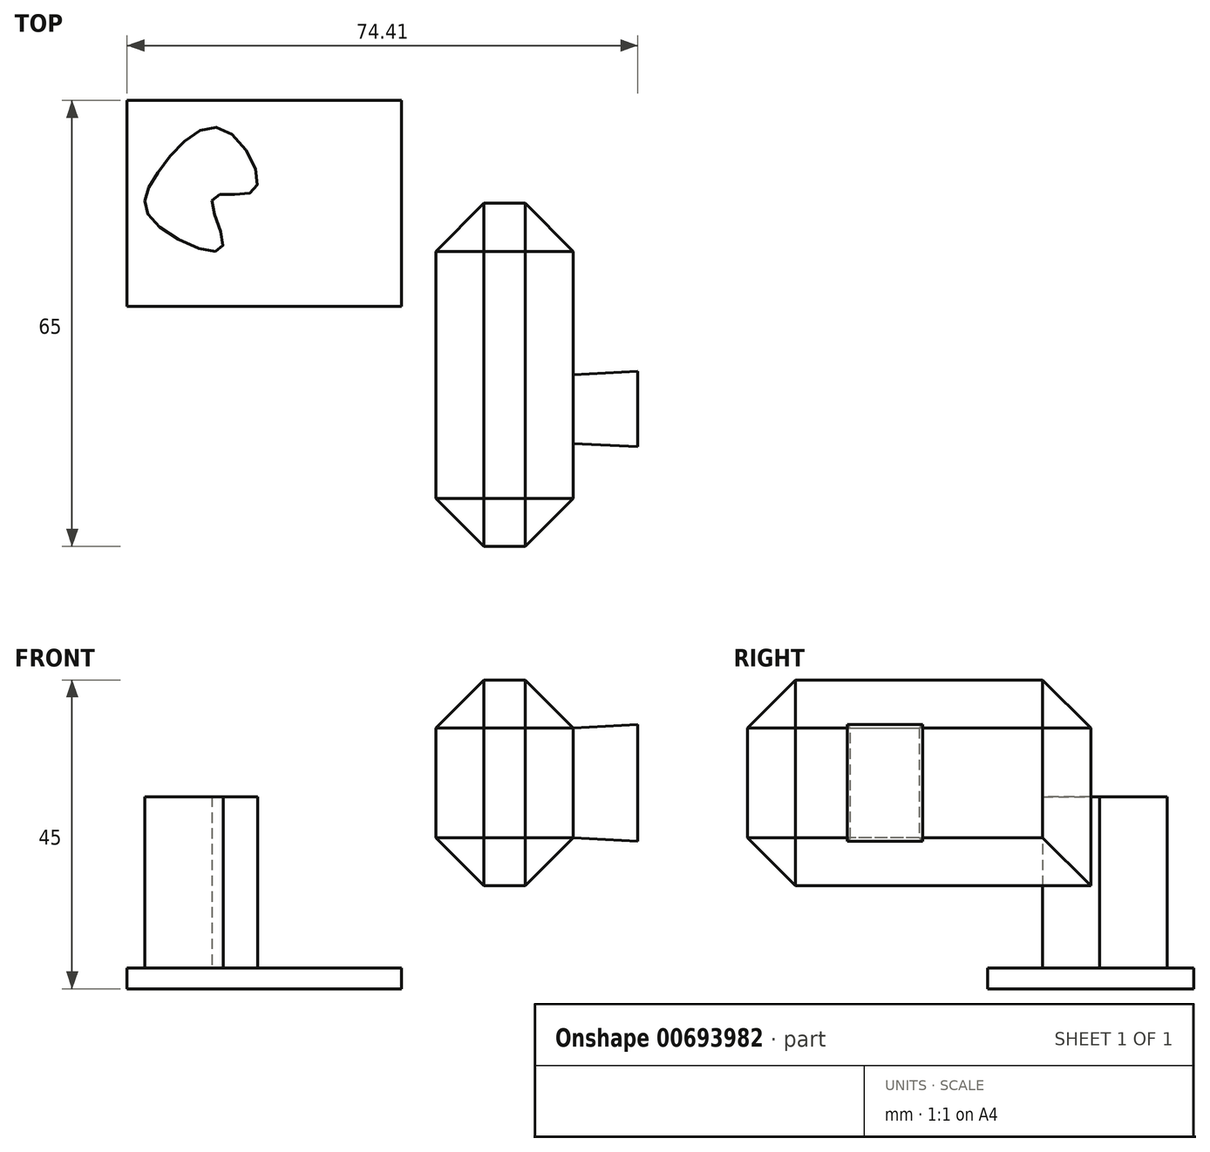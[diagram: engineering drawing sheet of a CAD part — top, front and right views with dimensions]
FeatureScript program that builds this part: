
annotation { "Feature Type Name" : "Feature", "Feature Type Description" : "" }
export const myFeature = defineFeature(function(context is Context, id is Id, definition is map)
    precondition{}
    {
        {
            var Q0;
            Q0=qCreatedBy(makeId("Top.planeOp"),FACE);
            var sketch = newSketch(context, id + "F0", { "sketchPlane" : qUnion([Q0])});
            skLineSegment(sketch, "E0.bottom", {"start": v(-50, 40) * mm, "end": v(-10, 40) * mm});
            skLineSegment(sketch, "E0.top", {"start": v(-50, 10) * mm, "end": v(-10, 10) * mm});
            skLineSegment(sketch, "E0.left", {"start": v(-50, 40) * mm, "end": v(-50, 10) * mm});
            skLineSegment(sketch, "E0.right", {"start": v(-10, 40) * mm, "end": v(-10, 10) * mm});
            skSolve(sketch);
        }
        {
            var Q0;
            Q0=makeQuery(id+"F0.imprint","IMPRINT",FACE,{"disambiguationData":[TD([[makeQuery(id+"F0.imprint","IMPRINT",EDGE,{"derivedFrom":sQuery(id+"F0.wireOp",EDGE,"E0.bottom")}),-1.0]])]});
            extrude(context, id + "F1", {"entities" : qUnion([Q0]), "depth" : 3 * mm, "offsetDistance" : 25 * mm});
        }
        {
            var Q0;
            Q0=qCreatedBy(makeId("Front.planeOp"),FACE);
            var sketch = newSketch(context, id + "F2", { "sketchPlane" : qUnion([Q0])});
            skLineSegment(sketch, "E1.bottom", {"start": v(-5, 45) * mm, "end": v(15, 45) * mm});
            skLineSegment(sketch, "E1.top", {"start": v(-5, 15) * mm, "end": v(15, 15) * mm});
            skLineSegment(sketch, "E1.left", {"start": v(-5, 45) * mm, "end": v(-5, 15) * mm});
            skLineSegment(sketch, "E1.right", {"start": v(15, 45) * mm, "end": v(15, 15) * mm});
            skSolve(sketch);
        }
        {
            var Q0;
            Q0=makeQuery(id+"F2.imprint","IMPRINT",FACE,{"disambiguationData":[TD([[makeQuery(id+"F2.imprint","IMPRINT",EDGE,{"derivedFrom":sQuery(id+"F2.wireOp",EDGE,"E1.bottom")}),-1.0]])]});
            extrude(context, id + "F3", {"entities" : qUnion([Q0]), "endBound" : BoundingType.SYMMETRIC, "depth" : 50 * mm, "offsetDistance" : 25 * mm});
        }
        {
            var Q0;
            Q0=makeQuery(id+"F3.opExtrude","CAP_FACE",FACE,{"disambiguationData":[OSD([sQuery(id+"F2.wireOp",EDGE,"E1.bottom"),sQuery(id+"F2.wireOp",EDGE,"E1.top"),sQuery(id+"F2.wireOp",EDGE,"E1.left"),sQuery(id+"F2.wireOp",EDGE,"E1.right")])],"isStart":false});
            var Q1;
            Q1=makeQuery(id+"F3.opExtrude","SWEPT_FACE",FACE,{"disambiguationData":[OSD([sQuery(id+"F2.wireOp",EDGE,"E1.bottom")])]});
            var Q2;
            Q2=makeQuery(id+"F3.opExtrude","SWEPT_FACE",FACE,{"disambiguationData":[OSD([sQuery(id+"F2.wireOp",EDGE,"E1.right")])]});
            var Q3;
            Q3=makeQuery(id+"F3.opExtrude","SWEPT_FACE",FACE,{"disambiguationData":[OSD([sQuery(id+"F2.wireOp",EDGE,"E1.left")])]});
            chamfer(context, id + "F4", {"entities" : qUnion([Q0, Q1, Q2, Q3]), "width" : 7 * mm});
        }
        {
            var Q0;
            Q0=makeQuery(id+"F1.opExtrude","CAP_FACE",FACE,{"disambiguationData":[OSD([sQuery(id+"F0.wireOp",EDGE,"E0.bottom"),sQuery(id+"F0.wireOp",EDGE,"E0.top"),sQuery(id+"F0.wireOp",EDGE,"E0.left"),sQuery(id+"F0.wireOp",EDGE,"E0.right")])],"isStart":false});
            var sketch = newSketch(context, id + "F5", { "sketchPlane" : qUnion([Q0])});
            skFitSpline(sketch, "E2", {"points": [v(-45.5, 29.5) * mm, v(-46.46, 22.7) * mm, v(-36.17, 18.48) * mm, v(-37.48, 25.77) * mm, v(-31.4, 26.92) * mm, v(-36.17, 35.9) * mm, v(-45.5, 29.5) * mm]});
            skSolve(sketch);
        }
        {
            var Q0;
            Q0 = qSketchRegion(id + "F5", true);
            extrude(context, id + "F6", {"entities" : qUnion([Q0]), "operationType" : NewBodyOperationType.ADD, "depth" : 25 * mm, "offsetDistance" : 25 * mm});
        }
        {
            var Q0;
            Q0=makeQuery(id+"F3.opExtrude","SWEPT_FACE",FACE,{"disambiguationData":[OSD([sQuery(id+"F2.wireOp",EDGE,"E1.right")])]});
            var sketch = newSketch(context, id + "F7", { "sketchPlane" : qUnion([Q0])});
            skLineSegment(sketch, "E3.bottom", {"start": v(-10, 22) * mm, "end": v(0, 22) * mm});
            skLineSegment(sketch, "E3.top", {"start": v(-10, 38) * mm, "end": v(0, 38) * mm});
            skLineSegment(sketch, "E3.left", {"start": v(-10, 22) * mm, "end": v(-10, 38) * mm});
            skLineSegment(sketch, "E3.right", {"start": v(0, 22) * mm, "end": v(0, 38) * mm});
            skSolve(sketch);
        }
        {
            var Q0;
            Q0=makeQuery(id+"F7.imprint","IMPRINT",FACE,{"disambiguationData":[TD([[makeQuery(id+"F7.imprint","IMPRINT",EDGE,{"derivedFrom":sQuery(id+"F7.wireOp",EDGE,"E3.bottom")}),1.0]])]});
            extrude(context, id + "F8", {"entities" : qUnion([Q0]), "operationType" : NewBodyOperationType.ADD, "depth" : 9.4 * mm, "offsetDistance" : 25 * mm, "hasDraft" : true, "draftAngle" : 3 * degree});
        }
    });
